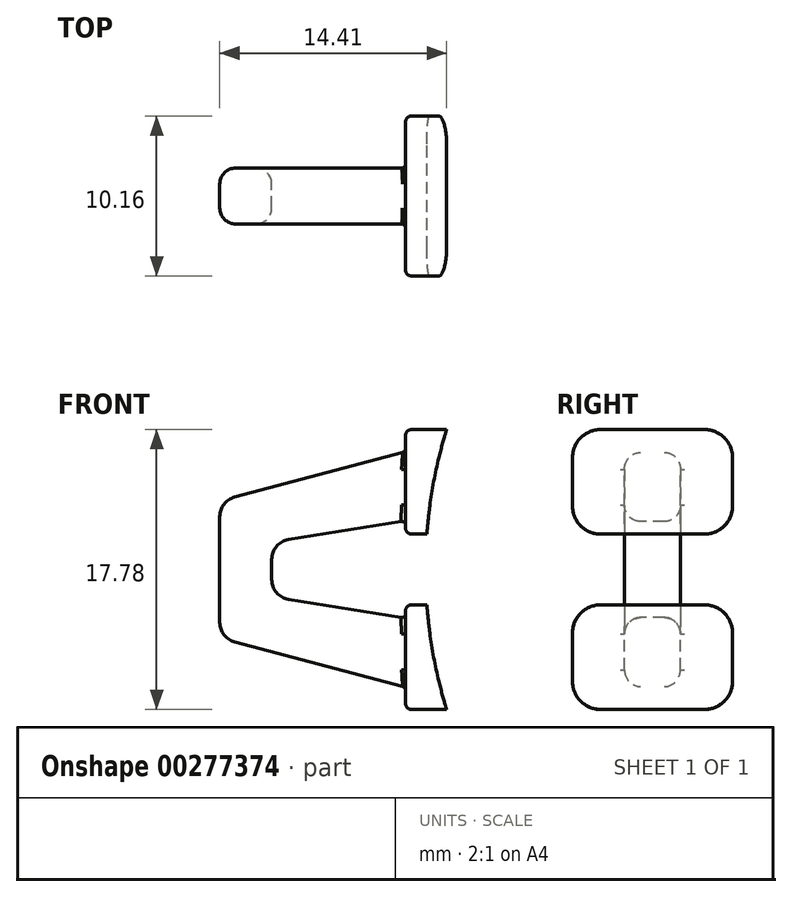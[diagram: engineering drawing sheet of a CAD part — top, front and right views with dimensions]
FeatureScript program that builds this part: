
annotation { "Feature Type Name" : "Feature", "Feature Type Description" : "" }
export const myFeature = defineFeature(function(context is Context, id is Id, definition is map)
    precondition{}
    {
        {
            var Q0;
            Q0=qCreatedBy(makeId("Front.planeOp"),FACE);
            var sketch = newSketch(context, id + "F0", { "sketchPlane" : qUnion([Q0])});
            skLineSegment(sketch, "E0", {"start": v(-28.89, -8.9) * mm, "end": v(-31.5, -8.9) * mm});
            skLineSegment(sketch, "E1", {"start": v(-31.5, -8.9) * mm, "end": v(-31.5, -7.48) * mm});
            skLineSegment(sketch, "E2", {"start": v(-31.5, -2.25) * mm, "end": v(-30.14, -2.25) * mm});
            skLineSegment(sketch, "E3.trimOffspring", {"start": v(-31.5, -3.1) * mm, "end": v(-31.5, -2.25) * mm});
            skLineSegment(sketch, "E4.MirrorCS", {"start": v(-31.5, 3.1) * mm, "end": v(-31.5, 2.25) * mm});
            skLineSegment(sketch, "E5.MirrorCS", {"start": v(-31.5, 8.9) * mm, "end": v(-31.5, 7.48) * mm});
            skLineSegment(sketch, "E6.MirrorCS", {"start": v(-28.89, 8.89) * mm, "end": v(-31.5, 8.89) * mm});
            skLineSegment(sketch, "E7.MirrorCS", {"start": v(-31.5, 2.25) * mm, "end": v(-30.14, 2.25) * mm});
            skArc(sketch, "E8", {"start": v(-30.14, -2.25) * mm, "mid": v(-29.7, -5.6) * mm, "end": v(-28.89, -8.9) * mm});
            skPoint(sketch, "E9.orphan", {"position": v(-29.04, 2.25) * mm});
            skPoint(sketch, "E10.orphan", {"position": v(-29.04, 8.9) * mm});
            skArc(sketch, "E11.trimOffspring", {"start": v(-28.89, 8.89) * mm, "mid": v(-29.7, 5.6) * mm, "end": v(-30.14, 2.25) * mm});
            skPoint(sketch, "E12.end.orphan", {"position": v(-29.04, -8.9) * mm});
            skPoint(sketch, "E12.start.orphan", {"position": v(-29.04, -2.25) * mm});
            skPoint(sketch, "E13.MirrorCS.end.orphan", {"position": v(-37.85, 0) * mm});
            skPoint(sketch, "E14.MirrorCS.end.orphan", {"position": v(-35.7, 0) * mm});
            skLineSegment(sketch, "E15", {"start": v(-31.5, -7.48) * mm, "end": v(-43.3, -4.35) * mm});
            skLineSegment(sketch, "E16", {"start": v(-43.3, -4.35) * mm, "end": v(-43.3, 0) * mm});
            skLineSegment(sketch, "E17", {"start": v(-40, 0) * mm, "end": v(-40, -1.73) * mm});
            skLineSegment(sketch, "E18", {"start": v(-40, -1.73) * mm, "end": v(-31.5, -3.1) * mm});
            skLineSegment(sketch, "E19.MirrorCS", {"start": v(-40, 0) * mm, "end": v(-40, 1.73) * mm});
            skLineSegment(sketch, "E20.MirrorCS", {"start": v(-43.3, 4.35) * mm, "end": v(-43.3, 0) * mm});
            skLineSegment(sketch, "E21.MirrorCS", {"start": v(-40, 1.73) * mm, "end": v(-31.5, 3.1) * mm});
            skLineSegment(sketch, "E22.MirrorCS", {"start": v(-31.5, 7.48) * mm, "end": v(-43.3, 4.35) * mm});
            skSolve(sketch);
        }
        {
            var Q0;
            Q0=qSketchRegion(id+"F0",true);
            extrude(context, id + "F1", {"entities" : qUnion([Q0]), "depth" : 3.56 * mm, "symmetric" : true});
        }
        {
            var Q0;
            Q0=qCreatedBy(makeId("Front.planeOp"),FACE);
            var sketch = newSketch(context, id + "F2", { "sketchPlane" : qUnion([Q0])});
            skLineSegment(sketch, "E23.bottom", {"start": v(-31.5, 8.89) * mm, "end": v(-28.89, 8.89) * mm});
            skLineSegment(sketch, "E23.top", {"start": v(-31.5, -8.9) * mm, "end": v(-28.89, -8.9) * mm});
            skLineSegment(sketch, "E23.left", {"start": v(-31.5, 8.89) * mm, "end": v(-31.5, 2.25) * mm});
            skLineSegment(sketch, "E24", {"start": v(-31.5, 2.25) * mm, "end": v(-30.14, 2.25) * mm});
            skLineSegment(sketch, "E25", {"start": v(-31.5, -2.25) * mm, "end": v(-30.14, -2.25) * mm});
            skArc(sketch, "E26", {"start": v(-28.89, 8.89) * mm, "mid": v(-29.7, 5.6) * mm, "end": v(-30.14, 2.25) * mm});
            skArc(sketch, "E27.trimOffspring", {"start": v(-30.14, -2.25) * mm, "mid": v(-29.7, -5.6) * mm, "end": v(-28.89, -8.9) * mm});
            skLineSegment(sketch, "E28.trimOffspring", {"start": v(-31.5, -2.25) * mm, "end": v(-31.5, -8.9) * mm});
            skSolve(sketch);
        }
        {
            var Q0;
            Q0=qSketchRegion(id+"F2",true);
            extrude(context, id + "F3", {"entities" : qUnion([Q0]), "operationType" : NewBodyOperationType.ADD, "depth" : 10.16 * mm, "symmetric" : true});
        }
        {
            var Q0;
            Q0=makeQuery(id+"F3.opExtrude","CAP_EDGE",EDGE,{"disambiguationData":[OSD([sQuery(id+"F2.wireOp",EDGE,"E23.bottom")])],"isStart":false});
            var Q1;
            Q1=makeQuery(id+"F3.opExtrude","CAP_EDGE",EDGE,{"disambiguationData":[OSD([sQuery(id+"F2.wireOp",EDGE,"E24")])],"isStart":false});
            var Q2;
            Q2=makeQuery(id+"F3.opExtrude","CAP_EDGE",EDGE,{"disambiguationData":[OSD([sQuery(id+"F2.wireOp",EDGE,"E23.bottom")])],"isStart":true});
            var Q3;
            Q3=makeQuery(id+"F3.opExtrude","CAP_EDGE",EDGE,{"disambiguationData":[OSD([sQuery(id+"F2.wireOp",EDGE,"E24")])],"isStart":true});
            var Q4;
            Q4=makeQuery(id+"F3.opExtrude","CAP_EDGE",EDGE,{"disambiguationData":[OSD([sQuery(id+"F2.wireOp",EDGE,"E25")])],"isStart":true});
            var Q5;
            Q5=makeQuery(id+"F3.opExtrude","CAP_EDGE",EDGE,{"disambiguationData":[OSD([sQuery(id+"F2.wireOp",EDGE,"E23.top")])],"isStart":true});
            var Q6;
            Q6=makeQuery(id+"F3.opExtrude","CAP_EDGE",EDGE,{"disambiguationData":[OSD([sQuery(id+"F2.wireOp",EDGE,"E23.top")])],"isStart":false});
            var Q7;
            Q7=makeQuery(id+"F3.opExtrude","CAP_EDGE",EDGE,{"disambiguationData":[OSD([sQuery(id+"F2.wireOp",EDGE,"E25")])],"isStart":false});
            fillet(context, id + "F4", {"entities" : qUnion([Q0, Q1, Q2, Q3, Q4, Q5, Q6, Q7]), "radius" : 1.78 * mm, "tangentPropagation" : true, "allowEdgeOverflow" : false});
        }
        {
            var Q0;
            Q0=makeQuery(id+"F3.opExtrude","SWEPT_EDGE",EDGE,{"disambiguationData":[OSD([sQuery(id+"F2.wireOp",EDGE,"E23.left"),sQuery(id+"F2.wireOp",EDGE,"E24")])]});
            var Q1;
            Q1=makeQuery(id+"F4.opFillet","BLEND_EDGE",EDGE,{"blendedFrom":[makeQuery(id+"F3.opExtrude","CAP_EDGE",EDGE,{"disambiguationData":[OSD([sQuery(id+"F2.wireOp",EDGE,"E24")])],"isStart":true}),makeQuery(id+"F3.boolean.opBoolean","MERGE",FACE,{"derivedFrom":[makeQuery(id+"F1.opExtrude","SWEPT_FACE",FACE,{"disambiguationData":[OSD([sQuery(id+"F0.wireOp",EDGE,"E4.MirrorCS")])]}),makeQuery(id+"F1.opExtrude","SWEPT_FACE",FACE,{"disambiguationData":[OSD([sQuery(id+"F0.wireOp",EDGE,"E5.MirrorCS")])]}),makeQuery(id+"F3.opExtrude","SWEPT_FACE",FACE,{"disambiguationData":[OSD([sQuery(id+"F2.wireOp",EDGE,"E23.left")])]})]})],"blendedInto":[makeQuery(id+"F3.boolean.opBoolean","MERGE",FACE,{"derivedFrom":[makeQuery(id+"F1.opExtrude","SWEPT_FACE",FACE,{"disambiguationData":[OSD([sQuery(id+"F0.wireOp",EDGE,"E4.MirrorCS")])]}),makeQuery(id+"F1.opExtrude","SWEPT_FACE",FACE,{"disambiguationData":[OSD([sQuery(id+"F0.wireOp",EDGE,"E5.MirrorCS")])]}),makeQuery(id+"F3.opExtrude","SWEPT_FACE",FACE,{"disambiguationData":[OSD([sQuery(id+"F2.wireOp",EDGE,"E23.left")])]})]})]});
            var Q2;
            Q2=makeQuery(id+"F3.opExtrude","CAP_EDGE",EDGE,{"disambiguationData":[OSD([sQuery(id+"F2.wireOp",EDGE,"E23.left")])],"isStart":true});
            var Q3;
            Q3=makeQuery(id+"F4.opFillet","BLEND_EDGE",EDGE,{"blendedFrom":[makeQuery(id+"F3.opExtrude","CAP_EDGE",EDGE,{"disambiguationData":[OSD([sQuery(id+"F2.wireOp",EDGE,"E23.bottom")])],"isStart":true}),makeQuery(id+"F3.boolean.opBoolean","MERGE",FACE,{"derivedFrom":[makeQuery(id+"F1.opExtrude","SWEPT_FACE",FACE,{"disambiguationData":[OSD([sQuery(id+"F0.wireOp",EDGE,"E4.MirrorCS")])]}),makeQuery(id+"F1.opExtrude","SWEPT_FACE",FACE,{"disambiguationData":[OSD([sQuery(id+"F0.wireOp",EDGE,"E5.MirrorCS")])]}),makeQuery(id+"F3.opExtrude","SWEPT_FACE",FACE,{"disambiguationData":[OSD([sQuery(id+"F2.wireOp",EDGE,"E23.left")])]})]})],"blendedInto":[makeQuery(id+"F3.boolean.opBoolean","MERGE",FACE,{"derivedFrom":[makeQuery(id+"F1.opExtrude","SWEPT_FACE",FACE,{"disambiguationData":[OSD([sQuery(id+"F0.wireOp",EDGE,"E4.MirrorCS")])]}),makeQuery(id+"F1.opExtrude","SWEPT_FACE",FACE,{"disambiguationData":[OSD([sQuery(id+"F0.wireOp",EDGE,"E5.MirrorCS")])]}),makeQuery(id+"F3.opExtrude","SWEPT_FACE",FACE,{"disambiguationData":[OSD([sQuery(id+"F2.wireOp",EDGE,"E23.left")])]})]})]});
            var Q4;
            Q4=makeQuery(id+"F3.opExtrude","CAP_EDGE",EDGE,{"disambiguationData":[OSD([sQuery(id+"F2.wireOp",EDGE,"E23.left")])],"isStart":true});
            var Q5;
            Q5=makeQuery(id+"F3.boolean.opBoolean","MERGE",EDGE,{"derivedFrom":[makeQuery(id+"F1.opExtrude","SWEPT_EDGE",EDGE,{"disambiguationData":[OSD([sQuery(id+"F0.wireOp",EDGE,"E5.MirrorCS"),sQuery(id+"F0.wireOp",EDGE,"E6.MirrorCS")])]}),makeQuery(id+"F3.opExtrude","SWEPT_EDGE",EDGE,{"disambiguationData":[OSD([sQuery(id+"F2.wireOp",EDGE,"E23.bottom"),sQuery(id+"F2.wireOp",EDGE,"E23.left")])]})]});
            var Q6;
            Q6=makeQuery(id+"F3.opExtrude","SWEPT_EDGE",EDGE,{"disambiguationData":[OSD([sQuery(id+"F2.wireOp",EDGE,"E25"),sQuery(id+"F2.wireOp",EDGE,"E28.trimOffspring")])]});
            fillet(context, id + "F5", {"entities" : qUnion([Q0, Q1, Q2, Q3, Q4, Q5, Q6]), "radius" : 0.38 * mm, "tangentPropagation" : true, "allowEdgeOverflow" : false});
        }
        {
            var Q0;
            Q0=makeQuery(id+"F1.opExtrude","SWEPT_EDGE",EDGE,{"disambiguationData":[OSD([sQuery(id+"F0.wireOp",EDGE,"E15"),sQuery(id+"F0.wireOp",EDGE,"E16")])]});
            var Q1;
            Q1=makeQuery(id+"F1.opExtrude","SWEPT_EDGE",EDGE,{"disambiguationData":[OSD([sQuery(id+"F0.wireOp",EDGE,"E20.MirrorCS"),sQuery(id+"F0.wireOp",EDGE,"E22.MirrorCS")])]});
            var Q2;
            Q2=makeQuery(id+"F1.opExtrude","SWEPT_EDGE",EDGE,{"disambiguationData":[OSD([sQuery(id+"F0.wireOp",EDGE,"E19.MirrorCS"),sQuery(id+"F0.wireOp",EDGE,"E21.MirrorCS")])]});
            var Q3;
            Q3=makeQuery(id+"F1.opExtrude","SWEPT_EDGE",EDGE,{"disambiguationData":[OSD([sQuery(id+"F0.wireOp",EDGE,"E17"),sQuery(id+"F0.wireOp",EDGE,"E18")])]});
            fillet(context, id + "F6", {"entities" : qUnion([Q0, Q1, Q2, Q3]), "radius" : 1.27 * mm, "tangentPropagation" : true, "allowEdgeOverflow" : false});
        }
        {
            var Q0;
            Q0=makeQuery(id+"F1.opExtrude","CAP_EDGE",EDGE,{"disambiguationData":[OSD([sQuery(id+"F0.wireOp",EDGE,"E15")])],"isStart":false});
            var Q1;
            Q1=makeQuery(id+"F1.opExtrude","CAP_EDGE",EDGE,{"disambiguationData":[OSD([sQuery(id+"F0.wireOp",EDGE,"E15")])],"isStart":true});
            var Q2;
            Q2=makeQuery(id+"F1.opExtrude","CAP_EDGE",EDGE,{"disambiguationData":[OSD([sQuery(id+"F0.wireOp",EDGE,"E17"),sQuery(id+"F0.wireOp",EDGE,"E19.MirrorCS")])],"isStart":false});
            var Q3;
            Q3=makeQuery(id+"F1.opExtrude","CAP_EDGE",EDGE,{"disambiguationData":[OSD([sQuery(id+"F0.wireOp",EDGE,"E21.MirrorCS")])],"isStart":true});
            fillet(context, id + "F7", {"entities" : qUnion([Q0, Q1, Q2, Q3]), "radius" : 1.02 * mm, "tangentPropagation" : true, "allowEdgeOverflow" : false});
        }
        {
            var Q0;
            Q0=makeQuery(id+"F3.boolean.opBoolean","INTERSECT",EDGE,{"derivedFrom":[makeQuery(id+"F1.opExtrude","CAP_FACE",FACE,{"disambiguationData":[OSD([sQuery(id+"F0.wireOp",EDGE,"E0"),sQuery(id+"F0.wireOp",EDGE,"E1"),sQuery(id+"F0.wireOp",EDGE,"E2"),sQuery(id+"F0.wireOp",EDGE,"E3.trimOffspring"),sQuery(id+"F0.wireOp",EDGE,"E4.MirrorCS"),sQuery(id+"F0.wireOp",EDGE,"E5.MirrorCS"),sQuery(id+"F0.wireOp",EDGE,"E6.MirrorCS"),sQuery(id+"F0.wireOp",EDGE,"E7.MirrorCS"),sQuery(id+"F0.wireOp",EDGE,"E8"),sQuery(id+"F0.wireOp",EDGE,"E11.trimOffspring"),sQuery(id+"F0.wireOp",EDGE,"E15"),sQuery(id+"F0.wireOp",EDGE,"E16"),sQuery(id+"F0.wireOp",EDGE,"E17"),sQuery(id+"F0.wireOp",EDGE,"E18"),sQuery(id+"F0.wireOp",EDGE,"E19.MirrorCS"),sQuery(id+"F0.wireOp",EDGE,"E20.MirrorCS"),sQuery(id+"F0.wireOp",EDGE,"E21.MirrorCS"),sQuery(id+"F0.wireOp",EDGE,"E22.MirrorCS")])],"isStart":false}),makeQuery(id+"F3.opExtrude","SWEPT_FACE",FACE,{"disambiguationData":[OSD([sQuery(id+"F2.wireOp",EDGE,"E28.trimOffspring")])]})]});
            var Q1;
            Q1=makeQuery(id+"F3.boolean.opBoolean","INTERSECT",EDGE,{"derivedFrom":[makeQuery(id+"F1.opExtrude","CAP_FACE",FACE,{"disambiguationData":[OSD([sQuery(id+"F0.wireOp",EDGE,"E0"),sQuery(id+"F0.wireOp",EDGE,"E1"),sQuery(id+"F0.wireOp",EDGE,"E2"),sQuery(id+"F0.wireOp",EDGE,"E3.trimOffspring"),sQuery(id+"F0.wireOp",EDGE,"E4.MirrorCS"),sQuery(id+"F0.wireOp",EDGE,"E5.MirrorCS"),sQuery(id+"F0.wireOp",EDGE,"E6.MirrorCS"),sQuery(id+"F0.wireOp",EDGE,"E7.MirrorCS"),sQuery(id+"F0.wireOp",EDGE,"E8"),sQuery(id+"F0.wireOp",EDGE,"E11.trimOffspring"),sQuery(id+"F0.wireOp",EDGE,"E15"),sQuery(id+"F0.wireOp",EDGE,"E16"),sQuery(id+"F0.wireOp",EDGE,"E17"),sQuery(id+"F0.wireOp",EDGE,"E18"),sQuery(id+"F0.wireOp",EDGE,"E19.MirrorCS"),sQuery(id+"F0.wireOp",EDGE,"E20.MirrorCS"),sQuery(id+"F0.wireOp",EDGE,"E21.MirrorCS"),sQuery(id+"F0.wireOp",EDGE,"E22.MirrorCS")])],"isStart":false}),makeQuery(id+"F3.opExtrude","SWEPT_FACE",FACE,{"disambiguationData":[OSD([sQuery(id+"F2.wireOp",EDGE,"E23.left")])]})]});
            fillet(context, id + "F8", {"entities" : qUnion([Q0, Q1]), "radius" : 0.25 * mm, "tangentPropagation" : true, "allowEdgeOverflow" : false});
        }
    });
